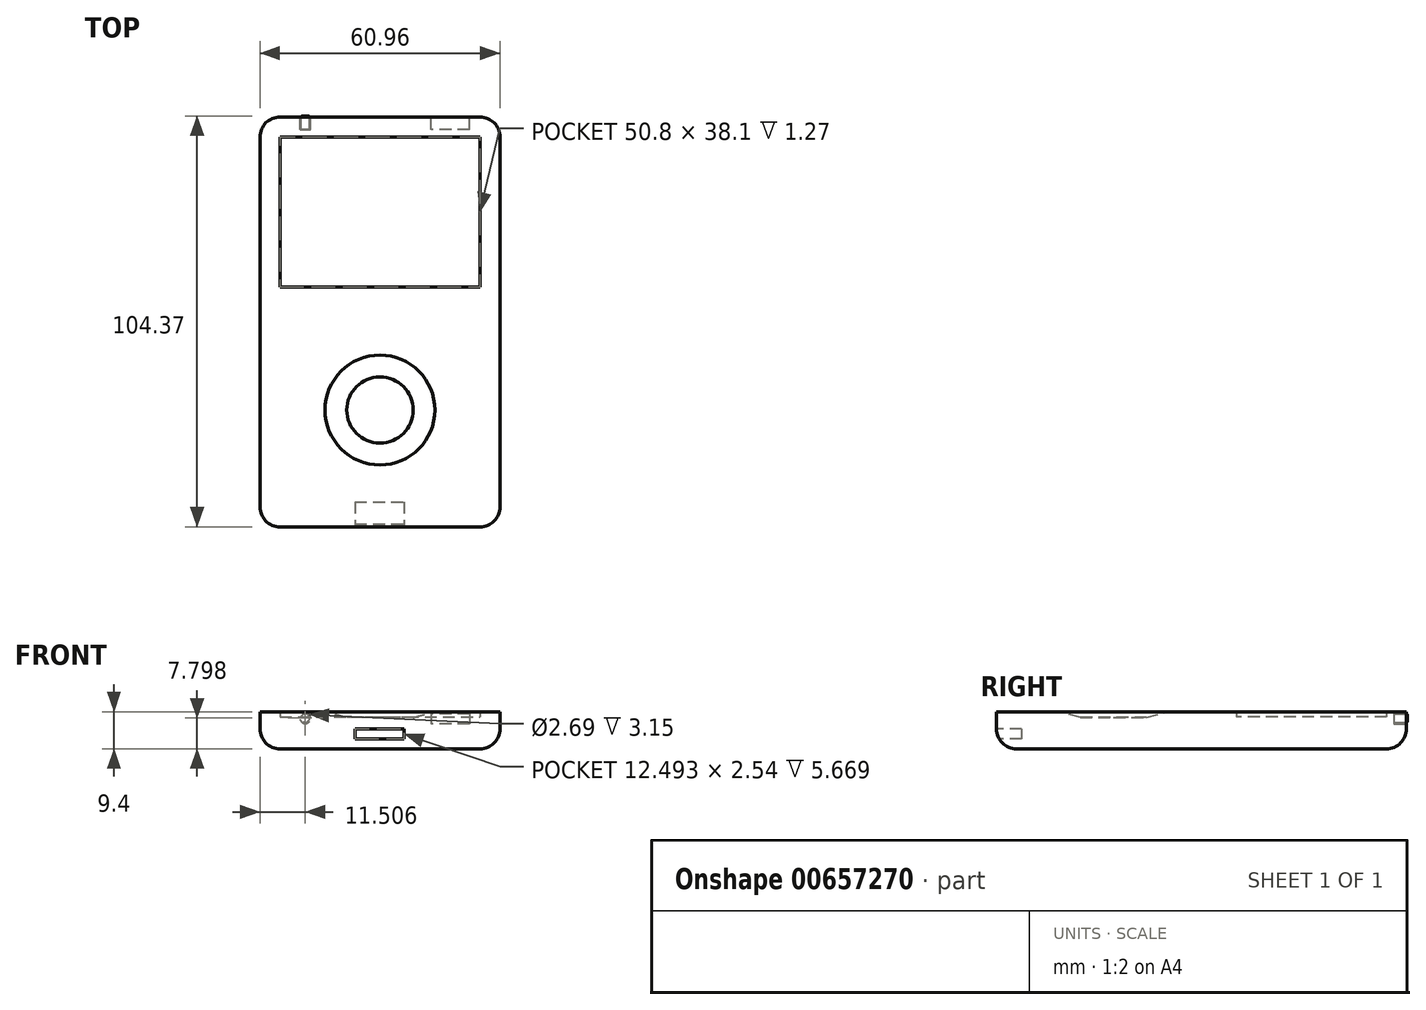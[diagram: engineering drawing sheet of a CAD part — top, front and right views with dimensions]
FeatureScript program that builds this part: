
annotation { "Feature Type Name" : "Feature", "Feature Type Description" : "" }
export const myFeature = defineFeature(function(context is Context, id is Id, definition is map)
    precondition{}
    {
        {
            var Q0;
            Q0=qCreatedBy(makeId("Top.planeOp"),FACE);
            var sketch = newSketch(context, id + "F0", { "sketchPlane" : qUnion([Q0])});
            skLineSegment(sketch, "E0.bottom", {"start": v(-25.4, 52.07) * mm, "end": v(25.4, 52.07) * mm});
            skLineSegment(sketch, "E0.top", {"start": v(-25.4, -52.07) * mm, "end": v(25.4, -52.07) * mm});
            skLineSegment(sketch, "E0.left", {"start": v(-30.48, 47) * mm, "end": v(-30.48, -47) * mm});
            skLineSegment(sketch, "E0.right", {"start": v(30.48, 47) * mm, "end": v(30.48, -47) * mm});
            skCircle(sketch, "E1", {"center": v(0, -21.59) * mm, "radius": 17.78 * mm});
            skCircle(sketch, "E2", {"center": v(0, -21.59) * mm, "radius": 7.62 * mm});
            skPoint(sketch, "E3.visualSharp", {"position": v(-30.48, 52.07) * mm});
            skArc(sketch, "E3.filletArc", {"start": v(-25.4, 52.07) * mm, "mid": v(-29, 50.58) * mm, "end": v(-30.48, 47) * mm});
            skPoint(sketch, "E4.visualSharp", {"position": v(30.48, 52.07) * mm});
            skArc(sketch, "E4.filletArc", {"start": v(30.48, 47) * mm, "mid": v(29, 50.58) * mm, "end": v(25.4, 52.07) * mm});
            skPoint(sketch, "E5.visualSharp", {"position": v(30.48, -52.07) * mm});
            skArc(sketch, "E5.filletArc", {"start": v(25.4, -52.07) * mm, "mid": v(29, -50.58) * mm, "end": v(30.48, -47) * mm});
            skPoint(sketch, "E6.visualSharp", {"position": v(-30.48, -52.07) * mm});
            skArc(sketch, "E6.filletArc", {"start": v(-30.48, -47) * mm, "mid": v(-29, -50.58) * mm, "end": v(-25.4, -52.07) * mm});
            skPoint(sketch, "E7", {"position": v(0, 52.07) * mm});
            skPoint(sketch, "E8", {"position": v(30.48, 0) * mm});
            skLineSegment(sketch, "E9.bottom", {"start": v(-25.4, 47) * mm, "end": v(25.4, 47) * mm});
            skLineSegment(sketch, "E9.top", {"start": v(-25.4, 8.9) * mm, "end": v(25.4, 8.9) * mm});
            skLineSegment(sketch, "E9.left", {"start": v(-25.4, 47) * mm, "end": v(-25.4, 8.9) * mm});
            skLineSegment(sketch, "E9.right", {"start": v(25.4, 47) * mm, "end": v(25.4, 8.9) * mm});
            skSolve(sketch);
        }
        {
            var Q0;
            Q0 = qSketchRegion(id + "F0", true);
            var Q1;
            Q1=makeQuery(id+"F0.imprint","IMPRINT",FACE,{"disambiguationData":[TD([[makeQuery(id+"F0.imprint","IMPRINT",EDGE,{"derivedFrom":sQuery(id+"F0.wireOp",EDGE,"E1")}),1.0]])]});
            var Q2;
            Q2=makeQuery(id+"F0.imprint","IMPRINT",FACE,{"disambiguationData":[TD([[makeQuery(id+"F0.imprint","IMPRINT",EDGE,{"derivedFrom":sQuery(id+"F0.wireOp",EDGE,"E2")}),1.0]])]});
            var Q3;
            Q3=makeQuery(id+"F0.imprint","IMPRINT",FACE,{"disambiguationData":[TD([[makeQuery(id+"F0.imprint","IMPRINT",EDGE,{"derivedFrom":sQuery(id+"F0.wireOp",EDGE,"E9.bottom")}),-1.0]])]});
            extrude(context, id + "F1", {"entities" : qUnion([Q0, Q1, Q2, Q3]), "depth" : 9.4 * mm, "offsetDistance" : 25.4 * mm});
        }
        {
            var Q0;
            Q0=makeQuery(id+"F1.opExtrude","SWEPT_FACE",FACE,{"disambiguationData":[OSD([sQuery(id+"F0.wireOp",EDGE,"E0.top")])]});
            var sketch = newSketch(context, id + "F2", { "sketchPlane" : qUnion([Q0])});
            skLineSegment(sketch, "E10.bottom", {"start": v(-6.34, 5.08) * mm, "end": v(6.15, 5.08) * mm});
            skLineSegment(sketch, "E10.top", {"start": v(-6.34, 2.54) * mm, "end": v(6.15, 2.54) * mm});
            skLineSegment(sketch, "E10.left", {"start": v(-6.34, 5.08) * mm, "end": v(-6.34, 2.54) * mm});
            skLineSegment(sketch, "E10.right", {"start": v(6.15, 5.08) * mm, "end": v(6.15, 2.54) * mm});
            skSolve(sketch);
        }
        {
            var Q0;
            Q0 = qSketchRegion(id + "F2", true);
            extrude(context, id + "F3", {"entities" : qUnion([Q0]), "operationType" : NewBodyOperationType.REMOVE, "oppositeDirection" : true, "depth" : 6.35 * mm, "offsetDistance" : 25.4 * mm});
        }
        {
            var Q0;
            Q0=makeQuery(id+"F1.opExtrude","SWEPT_FACE",FACE,{"disambiguationData":[OSD([sQuery(id+"F0.wireOp",EDGE,"E0.bottom")])]});
            var sketch = newSketch(context, id + "F4", { "sketchPlane" : qUnion([Q0])});
            skLineSegment(sketch, "E11.bottom", {"start": v(-22.73, 8.82) * mm, "end": v(-13.02, 8.82) * mm});
            skLineSegment(sketch, "E11.top", {"start": v(-22.73, 6.35) * mm, "end": v(-13.02, 6.35) * mm});
            skLineSegment(sketch, "E11.left", {"start": v(-22.73, 8.82) * mm, "end": v(-22.73, 6.35) * mm});
            skLineSegment(sketch, "E11.right", {"start": v(-13.02, 8.82) * mm, "end": v(-13.02, 6.35) * mm});
            skCircle(sketch, "E12", {"center": v(18.97, 7.8) * mm, "radius": 1.35 * mm});
            skCircle(sketch, "E13", {"center": v(18.97, 7.8) * mm, "radius": 1.09 * mm});
            skSolve(sketch);
        }
        {
            var Q0;
            Q0 = qSketchRegion(id + "F4", true);
            extrude(context, id + "F5", {"entities" : qUnion([Q0]), "operationType" : NewBodyOperationType.REMOVE, "oppositeDirection" : true, "depth" : 3.15 * mm, "offsetDistance" : 25.4 * mm});
        }
        {
            var Q0;
            Q0=makeQuery(id+"F5.boolean.opBoolean","SPLIT",FACE,{"disambiguationData":[TD([makeQuery(id+"F5.opExtrude","SWEPT_FACE",FACE,{"disambiguationData":[OSD([sQuery(id+"F4.wireOp",EDGE,"E13")])]})])],"derivedFrom":makeQuery(id+"F1.opExtrude","SWEPT_FACE",FACE,{"disambiguationData":[OSD([sQuery(id+"F0.wireOp",EDGE,"E0.bottom")])]})});
            extrude(context, id + "F6", {"entities" : qUnion([Q0]), "operationType" : NewBodyOperationType.ADD, "depth" : 0.23 * mm, "offsetDistance" : 25.4 * mm});
        }
        {
            var Q0;
            Q0=makeQuery(id+"F6.opExtrude","CAP_FACE",FACE,{"disambiguationData":[OSD([sQuery(id+"F0.wireOp",EDGE,"E0.bottom")])],"isStart":false});
            fillet(context, id + "F7", {"entities" : qUnion([Q0]), "radius" : 0.3 * mm, "tangentPropagation" : true, "allowEdgeOverflow" : false});
        }
        {
            var Q0;
            Q0=makeQuery(id+"F1.opExtrude","CAP_EDGE",EDGE,{"disambiguationData":[OSD([sQuery(id+"F0.wireOp",EDGE,"E6.filletArc")])],"isStart":true});
            fillet(context, id + "F8", {"entities" : qUnion([Q0]), "radius" : 5.08 * mm, "tangentPropagation" : true, "allowEdgeOverflow" : false});
        }
        {
            var Q0;
            Q0=makeQuery(id+"F0.imprint","IMPRINT",FACE,{"disambiguationData":[TD([[makeQuery(id+"F0.imprint","IMPRINT",EDGE,{"derivedFrom":sQuery(id+"F0.wireOp",EDGE,"E9.bottom")}),-1.0]])]});
            extrude(context, id + "F9", {"entities" : qUnion([Q0]), "operationType" : NewBodyOperationType.REMOVE, "depth" : 9.65 * mm, "offsetDistance" : 25.4 * mm, "hasSecondDirection" : true, "secondDirectionOppositeDirection" : false, "secondDirectionDepth" : 8.13 * mm});
        }
        {
            var Q0;
            Q0=qCreatedBy(makeId("Right.planeOp"),FACE);
            var sketch = newSketch(context, id + "F10", { "sketchPlane" : qUnion([Q0])});
            skLineSegment(sketch, "E14", {"start": v(-22.38, 0) * mm, "end": v(-22.38, 19.6) * mm, "construction": true});
            skLineSegment(sketch, "E15", {"start": v(-22.38, 10.12) * mm, "end": v(-22.38, 7.99) * mm});
            skLineSegment(sketch, "E16", {"start": v(-22.38, 7.99) * mm, "end": v(-13.95, 7.99) * mm});
            skLineSegment(sketch, "E17", {"start": v(-13.95, 7.99) * mm, "end": v(-7.62, 9.6) * mm});
            skLineSegment(sketch, "E18", {"start": v(-7.62, 9.6) * mm, "end": v(-22.38, 9.6) * mm});
            skSolve(sketch);
        }
        {
            var Q0;
            Q0 = qSketchRegion(id + "F10", true);
            var Q1;
            Q1=sQuery(id+"F10.wireOp",EDGE,"E14");
            revolve(context, id + "F11", {"operationType" : NewBodyOperationType.REMOVE, "entities" : qUnion([Q0]), "axis" : qUnion([Q1]), "revolveType" : RevolveType.FULL, "oppositeDirection" : true});
        }
    });
